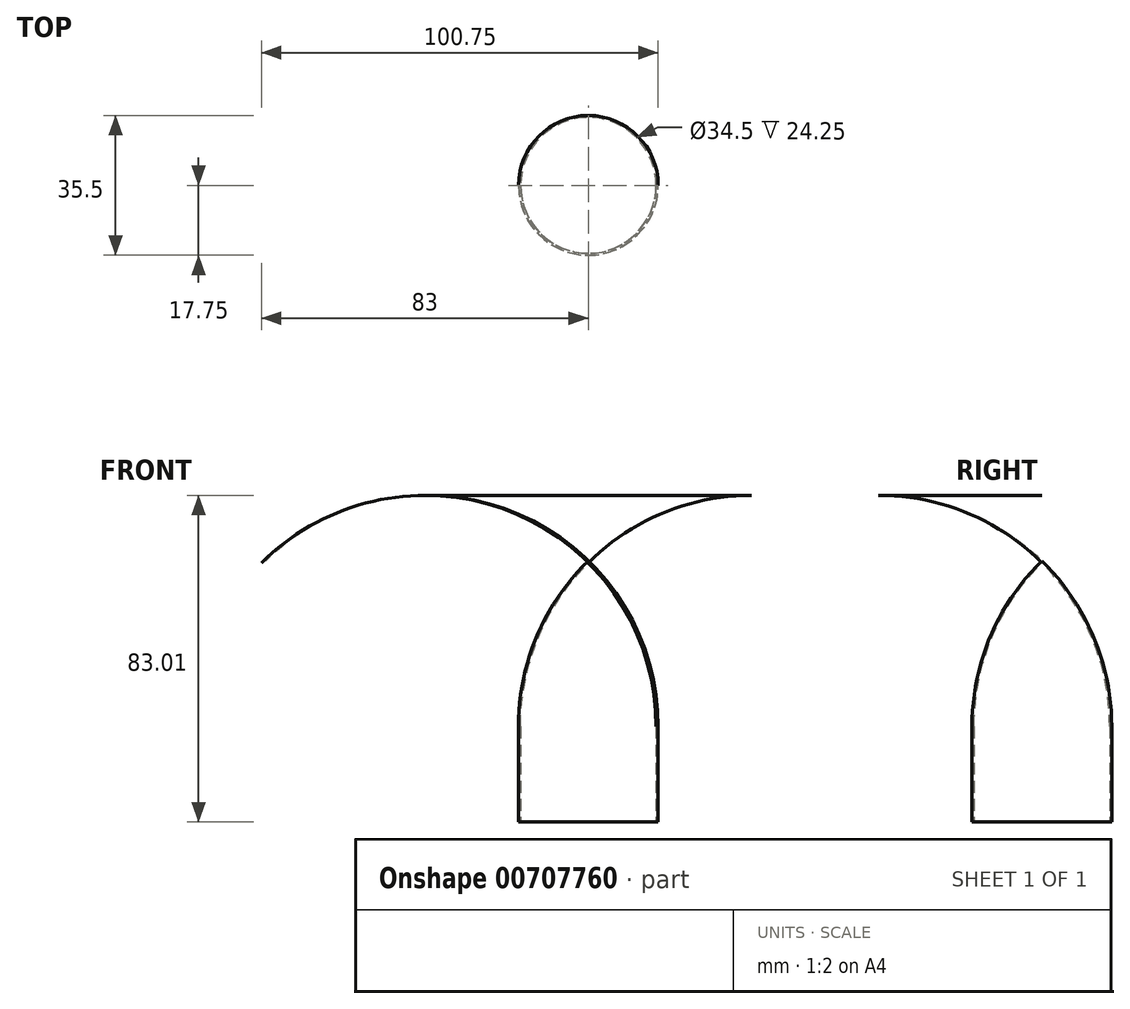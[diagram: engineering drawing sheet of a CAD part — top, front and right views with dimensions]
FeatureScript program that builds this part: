
annotation { "Feature Type Name" : "Feature", "Feature Type Description" : "" }
export const myFeature = defineFeature(function(context is Context, id is Id, definition is map)
    precondition{}
    {
        {
            var Q0;
            Q0=qCreatedBy(makeId("Front.planeOp"),FACE);
            var sketch = newSketch(context, id + "F0", { "sketchPlane" : qUnion([Q0])});
            skLineSegment(sketch, "E0.bottom", {"start": v(-17.25, -24.25) * mm, "end": v(-17.75, -24.25) * mm});
            skLineSegment(sketch, "E0.top", {"start": v(-17.25, 0) * mm, "end": v(-17.75, 0) * mm});
            skLineSegment(sketch, "E0.right", {"start": v(-17.75, -24.25) * mm, "end": v(-17.75, 0) * mm});
            skArc(sketch, "E1", {"start": v(0, 42.08) * mm, "mid": v(-13.13, 22.84) * mm, "end": v(-17.75, 0) * mm});
            skLineSegment(sketch, "E2.right", {"start": v(-17.25, 0) * mm, "end": v(-17.25, -21.75) * mm});
            skArc(sketch, "E3", {"start": v(0, 41.58) * mm, "mid": v(-12.77, 22.51) * mm, "end": v(-17.25, 0) * mm});
            skLineSegment(sketch, "E4", {"start": v(0, 41.58) * mm, "end": v(0, 42.08) * mm});
            skLineSegment(sketch, "E5", {"start": v(-17.25, -21.75) * mm, "end": v(-17.25, -24.25) * mm});
            skPoint(sketch, "E0.left.end.orphan", {"position": v(0, 0) * mm});
            skPoint(sketch, "E0.left.start.orphan", {"position": v(0, -24.25) * mm});
            skSolve(sketch);
        }
        {
            var Q0;
            Q0=qCreatedBy(makeId("Top.planeOp"),FACE);
            var sketch = newSketch(context, id + "F1", { "sketchPlane" : qUnion([Q0])});
            skCircle(sketch, "E6", {"center": v(0, 0) * mm, "radius": 17.3 * mm});
            skCircle(sketch, "E7", {"center": v(0, 0) * mm, "radius": 19.22 * mm});
            skSolve(sketch);
        }
        {
            var Q0;
            Q0=makeQuery(id+"F0.imprint","IMPRINT",FACE,{"disambiguationData":[TD([[makeQuery(id+"F0.imprint","IMPRINT",EDGE,{"derivedFrom":sQuery(id+"F0.wireOp",EDGE,"E0.top")}),-1.0]])]});
            var Q1;
            Q1=makeQuery(id+"F0.imprint","IMPRINT",FACE,{"disambiguationData":[TD([[makeQuery(id+"F0.imprint","IMPRINT",EDGE,{"derivedFrom":sQuery(id+"F0.wireOp",EDGE,"E0.bottom")}),-1.0]])]});
            var Q2;
            Q2=sQuery(id+"F1.wireOp",EDGE,"E6");
            revolve(context, id + "F2", {"surfaceOperationType" : NewSurfaceOperationType.NEW, "entities" : qUnion([Q0, Q1]), "axis" : qUnion([Q2]), "revolveType" : RevolveType.FULL});
        }
    });
